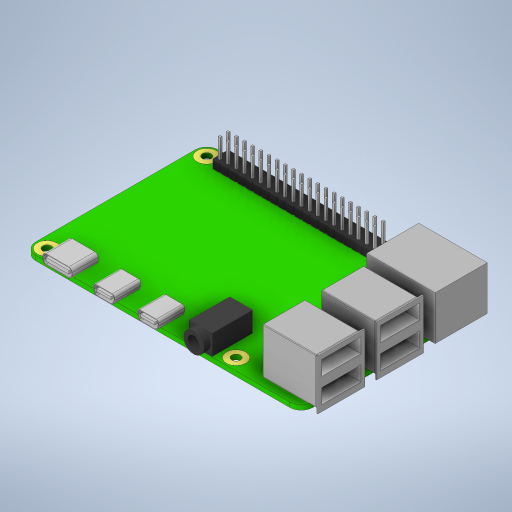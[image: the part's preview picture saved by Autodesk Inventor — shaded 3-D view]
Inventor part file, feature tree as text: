
AUTODESK INVENTOR PART (.ipt)
format: ipt  version: 2023.1 (Build 271208000, 208)  size: 1,098,752 bytes
history: native  units: mm
features: extrude x18, sketch x12, projected_geometry x4, pattern_linear x3, fillet x2, other x1, chamfer x1
ambient origin geometry x8: Origin, YZ Plane, XZ Plane, XY Plane, X Axis, Y Axis, Z Axis, Center Point
bodies: Body1 (feature_tree)
feature tree (41):
  other  "솔리드1"
  sketch  "스케치1"
  extrude  "돌출1"  Depth=85.0mm
  extrude  "돌출2"  Depth=56.0mm
  sketch  "스케치2"
  extrude  "돌출3"  Depth=2.7mm
  extrude  "돌출4"  Depth=6.0mm
  extrude  "돌출5"  Depth=3.5mm
  fillet  "모깎기1"  Radius=3.5mm
  fillet  "모깎기2"  Radius=3.5mm
  extrude  "돌출6"  Depth=20.0mm
  sketch  "스케치5"
  extrude  "돌출7"  Depth=3.5mm
  extrude  "돌출8"  Depth=1.5mm TaperAngle=0.0deg
  extrude  "돌출9"  Depth=1.51mm TaperAngle=0.0deg
  sketch  "스케치7"
  extrude  "돌출10"  Depth=45.75mm
  extrude  "돌출11"  Depth=27.0mm
  pattern_linear  "직사각형 패턴1"  Spacing1=9.0mm  [1 undecoded]
  extrude  "돌출12"  Depth=16.0mm
  extrude  "돌출13"  Depth=21.0mm
  chamfer  "모따기1"  Distance=13.0mm
  pattern_linear  "직사각형 패턴2"  Spacing1=17.5mm  [1 undecoded]
  sketch  "스케치11"
  extrude  "돌출14"  Depth=13.0mm
  extrude  "돌출15"  Depth=17.5mm
  extrude  "돌출16"  Depth=3.3mm
  extrude  "돌출17"  Depth=13.5mm TaperAngle=0.0deg
  extrude  "돌출18"  Depth=14.0mm TaperAngle=0.0deg
  pattern_linear  "직사각형 패턴3"  Spacing1=0.7mm  [1 undecoded]
  sketch  "스케치3"
  projected_geometry  "투영된 루프1"
  projected_geometry  "투영된 루프2"
  sketch  "스케치4"
  sketch  "스케치6"
  projected_geometry  "투영된 루프3"
  sketch  "스케치8"
  sketch  "스케치9"
  projected_geometry  "투영된 루프4"
  sketch  "스케치12"
  sketch  "스케치14"
note: 3 required parameter values undecoded (feature->parameter linkage not recoverable at this tier; creation-order binding heuristic only, values carry confidence <= 0.55)
